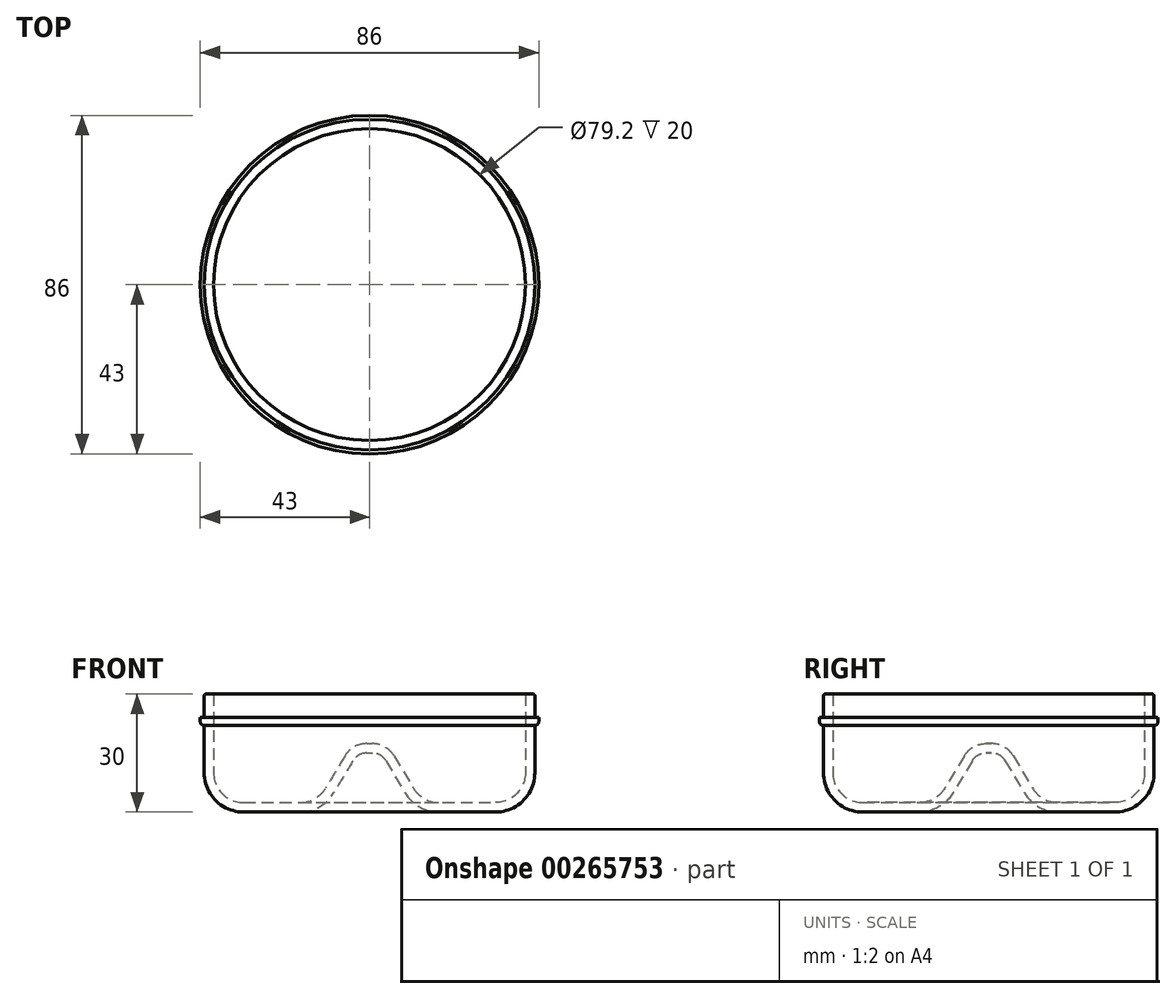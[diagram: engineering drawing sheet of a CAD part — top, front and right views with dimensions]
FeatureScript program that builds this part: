
annotation { "Feature Type Name" : "Feature", "Feature Type Description" : "" }
export const myFeature = defineFeature(function(context is Context, id is Id, definition is map)
    precondition{}
    {
        {
            var Q0;
            Q0=qCreatedBy(makeId("Front.planeOp"),FACE);
            var sketch = newSketch(context, id + "F0", { "sketchPlane" : qUnion([Q0])});
            skPoint(sketch, "E0", {"position": v(0, 15) * mm});
            skLineSegment(sketch, "E1", {"start": v(0, 15) * mm, "end": v(-0.74, 15) * mm});
            skLineSegment(sketch, "E2", {"start": v(-4.17, 13.06) * mm, "end": v(-9.09, 4.86) * mm});
            skLineSegment(sketch, "E3", {"start": v(-17.66, 0) * mm, "end": v(-32, 0) * mm});
            skLineSegment(sketch, "E4", {"start": v(-42, 10) * mm, "end": v(-42, 30) * mm});
            skPoint(sketch, "E5.visualSharp", {"position": v(-3, 15) * mm});
            skArc(sketch, "E5.filletArc", {"start": v(-0.74, 15) * mm, "mid": v(-2.7, 14.48) * mm, "end": v(-4.17, 13.06) * mm});
            skPoint(sketch, "E6.visualSharp", {"position": v(-12, 0) * mm});
            skArc(sketch, "E6.filletArc", {"start": v(-17.66, 0) * mm, "mid": v(-12.73, 1.3) * mm, "end": v(-9.09, 4.86) * mm});
            skPoint(sketch, "E7.visualSharp", {"position": v(-42, 0) * mm});
            skArc(sketch, "E7.filletArc", {"start": v(-42, 10) * mm, "mid": v(-39.07, 2.93) * mm, "end": v(-32, 0) * mm});
            skPoint(sketch, "E8", {"position": v(-42, 24) * mm});
            skPoint(sketch, "E9", {"position": v(-42, 22) * mm});
            skLineSegment(sketch, "E10", {"start": v(-42, 24) * mm, "end": v(-43, 24) * mm});
            skLineSegment(sketch, "E11", {"start": v(-43, 24) * mm, "end": v(-43, 23) * mm});
            skLineSegment(sketch, "E12", {"start": v(-42, 22) * mm, "end": v(-42, 22) * mm});
            skPoint(sketch, "E13.visualSharp", {"position": v(-43, 22) * mm});
            skArc(sketch, "E13.filletArc", {"start": v(-43, 23) * mm, "mid": v(-42.7, 22.3) * mm, "end": v(-42, 22) * mm});
            skLineSegment(sketch, "E14.0", {"start": v(-39.6, 10) * mm, "end": v(-39.6, 30) * mm});
            skArc(sketch, "E14.1", {"start": v(-39.6, 10) * mm, "mid": v(-37.37, 4.63) * mm, "end": v(-32, 2.4) * mm});
            skLineSegment(sketch, "E14.2", {"start": v(-17.66, 2.4) * mm, "end": v(-32, 2.4) * mm});
            skLineSegment(sketch, "E14.3", {"start": v(0, 17.4) * mm, "end": v(-0.74, 17.4) * mm});
            skArc(sketch, "E14.4", {"start": v(-0.74, 17.4) * mm, "mid": v(-3.89, 16.57) * mm, "end": v(-6.22, 14.3) * mm});
            skLineSegment(sketch, "E14.5", {"start": v(-6.22, 14.3) * mm, "end": v(-11.14, 6.09) * mm});
            skArc(sketch, "E14.6", {"start": v(-17.66, 2.4) * mm, "mid": v(-13.92, 3.39) * mm, "end": v(-11.14, 6.09) * mm});
            skLineSegment(sketch, "E15", {"start": v(-42, 30) * mm, "end": v(-39.6, 30) * mm});
            skLineSegment(sketch, "E16", {"start": v(0, 15) * mm, "end": v(0, 17.4) * mm});
            skSolve(sketch);
        }
        {
            var Q0;
            Q0=makeQuery(id+"F0.imprint","IMPRINT",FACE,{"disambiguationData":[TD([[makeQuery(id+"F0.imprint","IMPRINT",EDGE,{"derivedFrom":sQuery(id+"F0.wireOp",EDGE,"E1")}),-1.0]])]});
            var Q1;
            {var subQ0=sQuery(id+"F0.wireOp",EDGE,"E10");Q1=makeQuery(id+"F0.imprint","IMPRINT",FACE,{"disambiguationData":[TD([[makeQuery(id+"F0.imprint","IMPRINT",EDGE,{"derivedFrom":subQ0}),1.0]])]});}
            var Q2;
            Q2=sQuery(id+"F0.wireOp",EDGE,"E16");
            revolve(context, id + "F1", {"entities" : qUnion([Q0, Q1]), "axis" : qUnion([Q2]), "revolveType" : RevolveType.FULL});
        }
        {
            var Q0;
            Q0=makeQuery(id+"F1.opRevolve","SWEPT_EDGE",EDGE,{"disambiguationData":[OSD([sQuery(id+"F0.wireOp",EDGE,"E4"),sQuery(id+"F0.wireOp",EDGE,"E15")])]});
            fillet(context, id + "F2", {"entities" : qUnion([Q0]), "radius" : 0.5 * mm, "tangentPropagation" : true, "allowEdgeOverflow" : false});
        }
    });
